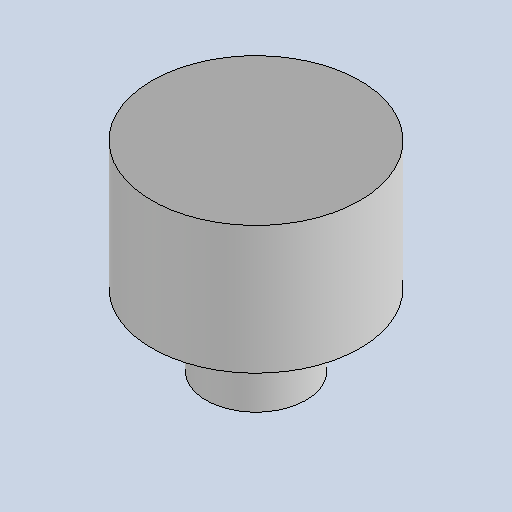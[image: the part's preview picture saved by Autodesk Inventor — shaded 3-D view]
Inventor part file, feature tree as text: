
AUTODESK INVENTOR PART (.ipt)
format: ipt  version: 2025 (Build 290162010, 162A)  size: 90,112 bytes
history: native  units: mm
features: revolve x1, sketch x1
ambient origin geometry x8: Origin, YZ Plane, XZ Plane, XY Plane, X Axis, Y Axis, Z Axis, Center Point
bodies: Solid1 (feature_tree)
feature tree (2):
  revolve  "Revolution1"  [1 undecoded]
  sketch  "Sketch1"  dims[d0=50.0mm d1=52.0mm d2=25.0mm d3=32.0mm d4=17.453293mm d5=90.0deg]
note: 1 required parameter value undecoded (feature->parameter linkage not recoverable at this tier; creation-order binding heuristic only, values carry confidence <= 0.55)
